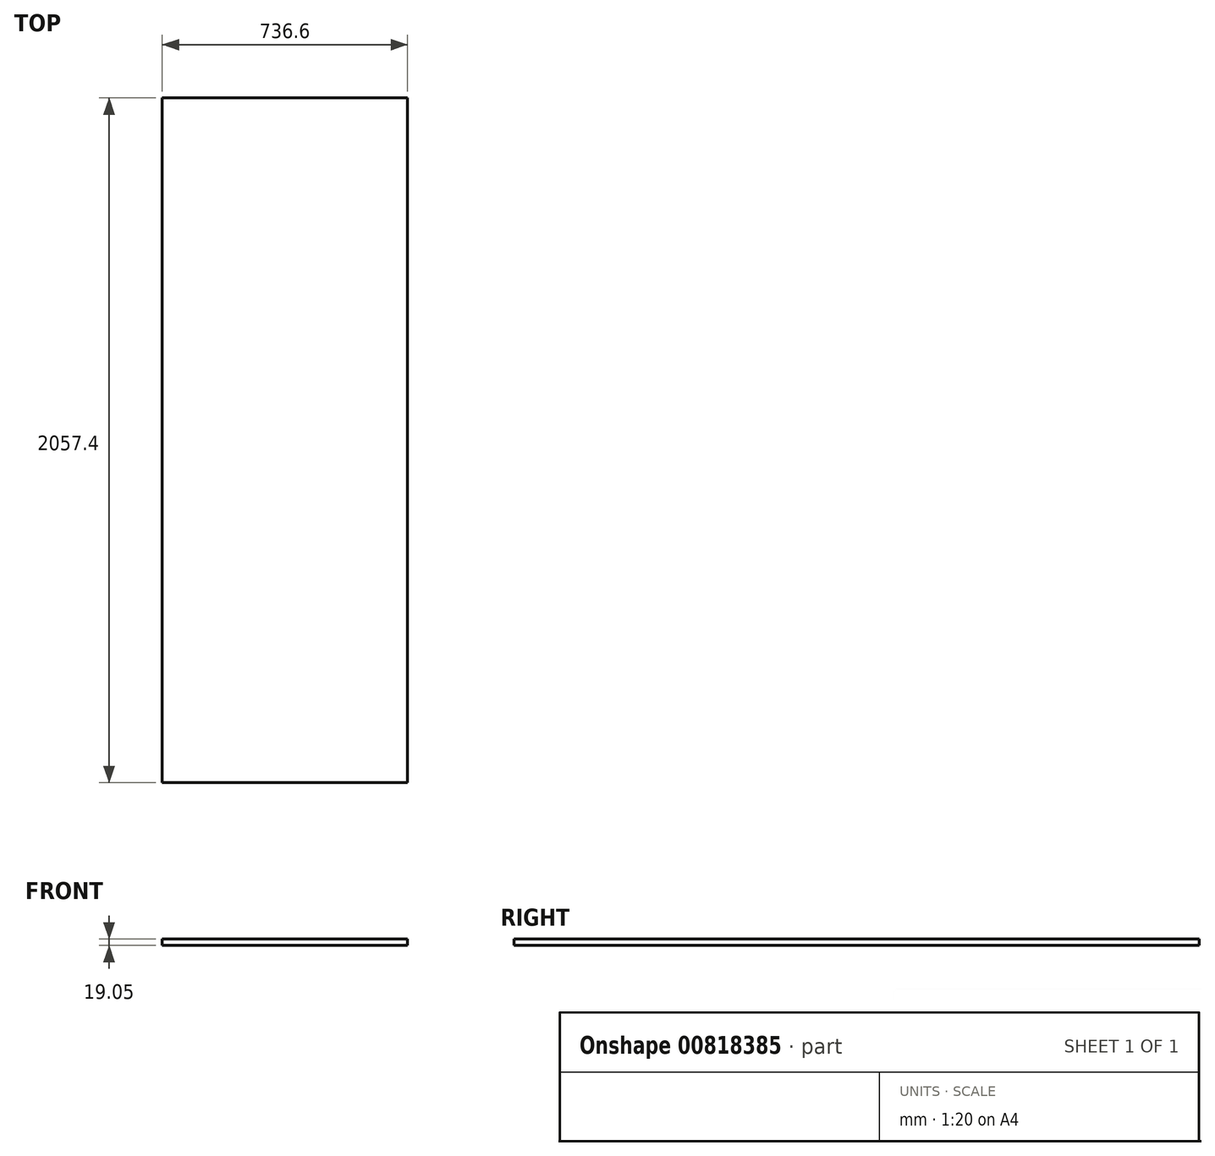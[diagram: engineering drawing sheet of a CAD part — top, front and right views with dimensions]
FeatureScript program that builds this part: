
annotation { "Feature Type Name" : "Feature", "Feature Type Description" : "" }
export const myFeature = defineFeature(function(context is Context, id is Id, definition is map)
    precondition{}
    {
        {
            var Q0;
            Q0=qCreatedBy(makeId("Top.planeOp"),FACE);
            var sketch = newSketch(context, id + "F0", { "sketchPlane" : qUnion([Q0])});
            skLineSegment(sketch, "E0.bottom", {"start": v(-368.3, -1028.7) * mm, "end": v(368.3, -1028.7) * mm});
            skLineSegment(sketch, "E0.top", {"start": v(-368.3, 1028.7) * mm, "end": v(368.3, 1028.7) * mm});
            skLineSegment(sketch, "E0.left", {"start": v(-368.3, -1028.7) * mm, "end": v(-368.3, 1028.7) * mm});
            skLineSegment(sketch, "E0.right", {"start": v(368.3, -1028.7) * mm, "end": v(368.3, 1028.7) * mm});
            skLineSegment(sketch, "E1", {"start": v(-368.3, 1028.7) * mm, "end": v(368.3, -1028.7) * mm, "construction": true});
            skSolve(sketch);
        }
        {
            var Q0;
            Q0 = qSketchRegion(id + "F0", true);
            extrude(context, id + "F1", {"entities" : qUnion([Q0]), "depth" : 19.05 * mm, "offsetDistance" : 25.4 * mm});
        }
    });
